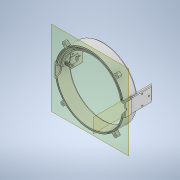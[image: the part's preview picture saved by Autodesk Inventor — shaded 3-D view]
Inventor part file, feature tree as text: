
AUTODESK INVENTOR PART (.ipt)
format: ipt  version: 2020.2 (Build 242310000, 310)  size: 914,432 bytes
history: native  units: mm
features: extrude x27, sketch x27, reference x21, other x8, plane x6, chamfer x3, pattern_circular x2, mirror x1, split x1, delete_face x1
ambient origin geometry x8: Origin, YZ Plane, XZ Plane, XY Plane, X Axis, Y Axis, Z Axis, Center Point
bodies: Solid1 (feature_tree), Solid2 (feature_tree), Solid3 (feature_tree)
feature tree (97):
  extrude  "Extrusion1"  Depth=205.0mm
  extrude  "Extrusion2"  Depth=40.0mm
  plane  "Work Plane4"
  extrude  "Extrusion3"  Depth=3.0mm TaperAngle=0.0deg
  extrude  "Extrusion4"  Depth=45.0mm
  extrude  "Extrusion6"  TaperAngle=0.0deg  [1 undecoded]
  extrude  "Extrusion8"  Depth=2.0mm
  chamfer  "Chamfer1"  Distance=20.0mm Angle=360.0deg
  pattern_circular  "Circular Pattern1"  Count=8  [1 undecoded]
  mirror  "Mirror1"
  plane  "Work Plane6"
  plane  "Work Plane8"
  extrude  "Extrusion15"  Depth=40.0mm
  extrude  "Extrusion16"  Depth=1.0mm
  extrude  "Extrusion17"  Depth=8.0mm
  extrude  "Extrusion20"  Depth=20.0mm TaperAngle=0.0deg
  chamfer  "Chamfer2"  Distance=5.0mm
  pattern_circular  "Circular Pattern2"  Count=2 Angle=360.0deg
  extrude  "Extrusion19"  Depth=191.666667mm
  extrude  "Extrusion21"  Depth=3.0mm TaperAngle=0.0deg
  extrude  "Extrusion22"  Depth=2.0mm
  extrude  "Extrusion23"  Depth=0.4mm
  extrude  "Extrusion24"  Depth=6.0mm
  plane  "Work Plane10"
  extrude  "Extrusion25"  TaperAngle=0.0deg  [1 undecoded]
  extrude  "Extrusion26"  TaperAngle=0.0deg  [1 undecoded]
  extrude  "Extrusion27"  Depth=6.0mm
  extrude  "Extrusion28"  Depth=5.0mm TaperAngle=0.0deg
  extrude  "Extrusion29"  Depth=5.0mm TaperAngle=0.0deg
  extrude  "Extrusion30"  Depth=5.0mm TaperAngle=0.0deg
  extrude  "Extrusion34"  Depth=2.0mm
  extrude  "Extrusion35"  Depth=2.0mm
  plane  "Work Plane11"
  extrude  "Extrusion36"  Depth=6.0mm TaperAngle=0.0deg
  extrude  "Extrusion37"  [1 undecoded]
  extrude  "Extrusion38"  Depth=5.0mm
  chamfer  "Chamfer3"  Distance=8.0mm
  split  "Split1"
  delete_face  "Delete Face1"
  extrude  "Extrusion40"  Depth=5.0mm
  sketch  "Sketch1"  dims[d0=215.0mm d1=205.0mm]
  sketch  "Sketch2"  dims[d2=40.0mm d3=0.0mm d4=208.633333mm]
  plane  "Work Plane3"
  sketch  "Sketch4"  dims[d5=211.366667mm d6=3.0mm d7=0.0mm]
  sketch  "Sketch5"  dims[d8=45.0mm d9=45.0mm]
  reference  "Reference1"
  sketch  "Sketch6"  dims[d10=3.0mm d11=0.0mm d12=0.0mm]
  sketch  "Sketch8"  dims[d13=2.0mm d14=0.0mm d17=0.1mm]
  reference  "Reference7"
  reference  "Reference8"
  reference  "Reference9"
  reference  "Reference10"
  sketch  "Sketch16"  dims[d18=1.9mm]
  sketch  "Sketch17"  dims[d19=0.0mm d23=20.0mm d24=360.0deg]
  reference  "Reference12"
  reference  "Reference13"
  sketch  "Sketch18"  dims[d26=0.1mm]
  sketch  "Sketch20"  dims[d27=1.0mm d28=0.0mm]
  sketch  "Sketch21"  dims[d29=2.0mm d30=2.0mm d31=45.0deg]
  sketch  "Sketch22"  dims[d67=30.2mm]
  sketch  "Sketch23"  dims[d68=41.0mm d69=80.0mm]
  reference  "Reference14"
  reference  "Reference15"
  sketch  "Sketch24"  dims[d70=40.0mm d71=20.5mm]
  sketch  "Sketch25"  dims[d72=215.0mm d73=0.0mm d74=1.0mm]
  reference  "Reference16"
  reference  "Reference17"
  sketch  "Sketch26"  dims[d75=4.0mm d76=8.0mm]
  reference  "Reference18"
  reference  "Reference19"
  sketch  "Sketch27"  dims[d77=26.0mm d78=20.0mm d79=0.0mm]
  reference  "Reference20"
  reference  "Reference21"
  sketch  "Sketch28"  dims[d80=10.0mm d83=5.0mm d84=0.0mm]
  sketch  "Sketch29"  dims[d85=0.0mm]
  reference  "Reference22"
  reference  "Reference23"
  reference  "Reference24"
  reference  "Reference25"
  sketch  "Sketch30"  dims[d86=2.5mm d87=0.0mm d97=20.0mm d98=360.0deg]
  reference  "Reference26"
  reference  "Reference27"
  sketch  "Sketch31"  dims[d100=215.0mm d101=0.0mm d102=191.666667mm]
  sketch  "Sketch35"  dims[d103=198.333333mm d104=3.0mm d105=0.0mm]
  sketch  "Sketch36"  dims[d106=2.0mm d107=2.0mm d108=45.0deg d110=20.0mm]
  sketch  "Sketch39"  dims[d111=72.5mm d112=0.0mm d114=0.4mm]
  sketch  "Sketch40"  dims[d115=6.0mm d116=6.8mm]
  sketch  "Sketch41"  dims[d117=6.8mm d118=0.0mm]
  sketch  "Sketch42"  dims[d119=0.0mm d120=0.0mm d121=6.0mm d122=4.0mm d123=0.0mm d124=7.5mm d125=0.0mm d126=3.0mm d127=0.0mm d128=2.0mm d129=2.0mm d130=6.0mm d131=0.0mm d132=-7.0mm d133=16.0mm d134=8.0mm d135=0.5mm d136=40.0mm d137=30.2mm d138=3.0mm d139=22.0mm d140=0.0mm d141=2.0mm d142=2.0mm d143=10.0mm d144=0.0mm d145=5.0mm d146=5.0mm d147=4.0mm d148=0.0mm d149=100.0mm d150=0.0mm d151=57.0mm d153=10.0mm d154=1.8mm d155=0.0mm d156=10.0mm d157=0.0mm d158=3.0mm d159=3.0mm d160=5.0mm d161=0.0mm d162=1.5mm d163=0.0mm d176=28.0mm d177=20.0mm d178=6.0mm d179=4.0mm d180=30.0mm d181=1.0mm d182=0.0mm d183=1.0mm d184=0.0mm d185=12.0mm d186=14.0mm d187=4.0mm d188=40.0mm d190=360.0deg d192=20.0mm d193=0.0mm d194=7.0mm d195=40.0mm d197=360.0deg d199=4.0mm d200=0.0mm d201=8.0mm d202=40.0mm d204=360.0deg d206=5.0mm d207=0.0mm d208=3.0mm d209=2.0mm d210=45.0deg d218=1.3mm d219=1.3mm d220=1.3mm d221=1.3mm d223=1.3mm d224=1.3mm d225=1.3mm d226=5.0mm d227=0.0mm d88=0.872665mm]
  other  "<userpath>\OneDrive\Apps\0011_VentControlValve\Assembly.iam"
  other  "Assembly.iam"
  other  "Base:1"
  other  "<userpath>\OneDrive\Apps\0011_VentControlValve\Drawings\Assembly.iam"
  other  "Butterfly Valve:1"
  other  "limitSwitch:2"
  other  "limitSwitch:1"
  other  "motor+Gearbox:1"
note: 5 required parameter values undecoded (feature->parameter linkage not recoverable at this tier; creation-order binding heuristic only, values carry confidence <= 0.55)
